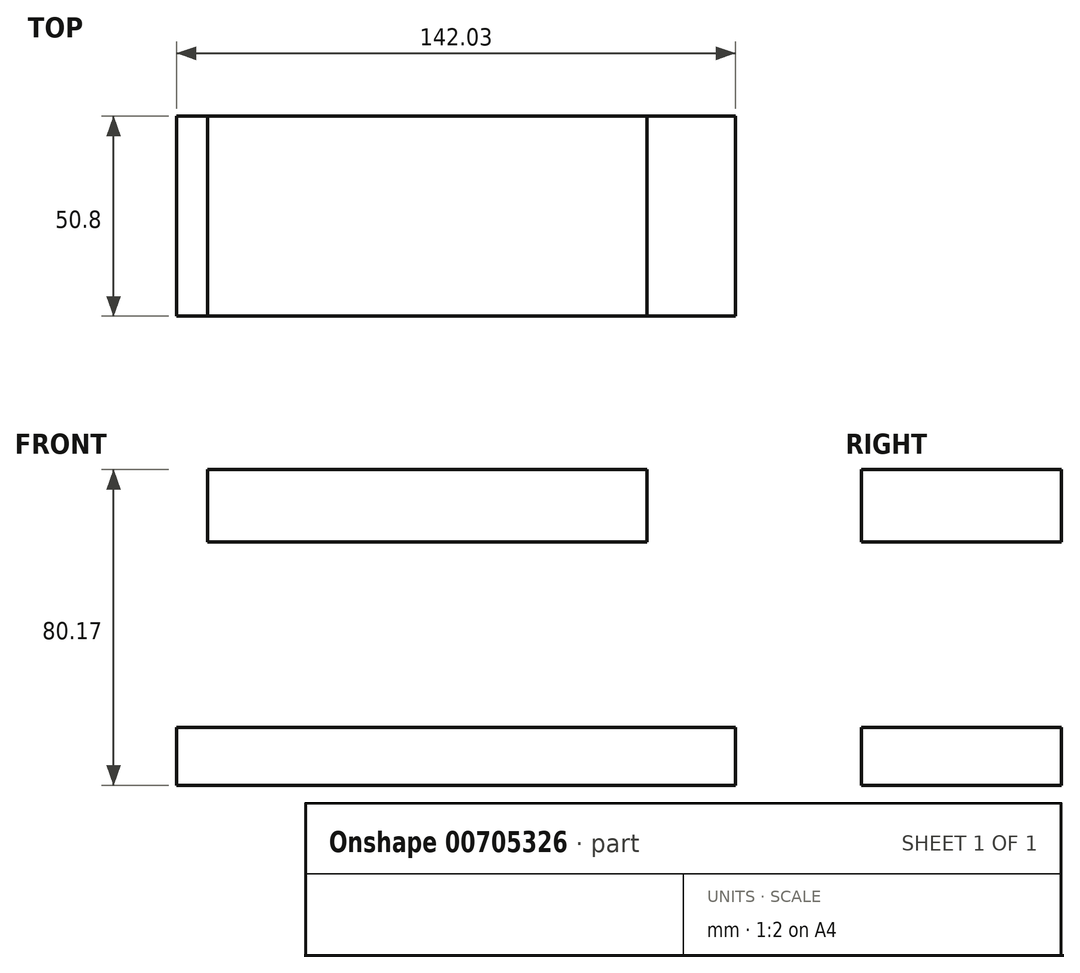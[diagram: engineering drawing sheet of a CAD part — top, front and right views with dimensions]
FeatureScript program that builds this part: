
annotation { "Feature Type Name" : "Feature", "Feature Type Description" : "" }
export const myFeature = defineFeature(function(context is Context, id is Id, definition is map)
    precondition{}
    {
        {
            var Q0;
            Q0=qCreatedBy(makeId("Front.planeOp"),FACE);
            var sketch = newSketch(context, id + "F0", { "sketchPlane" : qUnion([Q0])});
            skLineSegment(sketch, "E0.bottom", {"start": v(52.72, 35.9) * mm, "end": v(-58.98, 35.9) * mm});
            skLineSegment(sketch, "E0.top", {"start": v(52.72, 17.59) * mm, "end": v(-58.98, 17.59) * mm});
            skLineSegment(sketch, "E0.left", {"start": v(52.72, 35.9) * mm, "end": v(52.72, 17.59) * mm});
            skLineSegment(sketch, "E0.right", {"start": v(-58.98, 35.9) * mm, "end": v(-58.98, 17.59) * mm});
            skSolve(sketch);
        }
        {
            var Q0;
            Q0=makeQuery(id+"F0.imprint","IMPRINT",FACE,{"disambiguationData":[TD([[makeQuery(id+"F0.imprint","IMPRINT",EDGE,{"derivedFrom":sQuery(id+"F0.wireOp",EDGE,"E0.bottom")}),1.0]])]});
            extrude(context, id + "F1", {"entities" : qUnion([Q0]), "depth" : 25.4 * mm, "offsetDistance" : 25.4 * mm});
        }
        {
            var Q0;
            Q0=makeQuery(id+"F1.opExtrude","CAP_FACE",FACE,{"disambiguationData":[OSD([sQuery(id+"F0.wireOp",EDGE,"E0.bottom"),sQuery(id+"F0.wireOp",EDGE,"E0.top"),sQuery(id+"F0.wireOp",EDGE,"E0.left"),sQuery(id+"F0.wireOp",EDGE,"E0.right")])],"isStart":false});
            extrude(context, id + "F2", {"entities" : qUnion([Q0]), "operationType" : NewBodyOperationType.ADD, "depth" : 25.4 * mm, "offsetDistance" : 25.4 * mm});
        }
        {
            var Q0;
            Q0=qCreatedBy(makeId("Front.planeOp"),FACE);
            var sketch = newSketch(context, id + "F3", { "sketchPlane" : qUnion([Q0])});
            skLineSegment(sketch, "E1.right", {"start": v(70.44, -2.53) * mm, "end": v(70.44, 0) * mm});
            skLineSegment(sketch, "E2.bottom", {"start": v(-66.8, -29.56) * mm, "end": v(75.24, -29.56) * mm});
            skLineSegment(sketch, "E2.top", {"start": v(-66.8, -44.27) * mm, "end": v(75.24, -44.27) * mm});
            skLineSegment(sketch, "E2.left", {"start": v(-66.8, -29.56) * mm, "end": v(-66.8, -44.27) * mm});
            skLineSegment(sketch, "E2.right", {"start": v(75.24, -29.56) * mm, "end": v(75.24, -44.27) * mm});
            skSolve(sketch);
        }
        {
            var Q0;
            Q0=makeQuery(id+"F3.imprint","IMPRINT",FACE,{"disambiguationData":[TD([[makeQuery(id+"F3.imprint","IMPRINT",EDGE,{"derivedFrom":sQuery(id+"F3.wireOp",EDGE,"E2.bottom")}),-1.0]])]});
            extrude(context, id + "F4", {"entities" : qUnion([Q0]), "depth" : 25.4 * mm, "offsetDistance" : 25.4 * mm});
        }
        {
            var Q0;
            Q0=makeQuery(id+"F4.opExtrude","CAP_FACE",FACE,{"disambiguationData":[OSD([sQuery(id+"F3.wireOp",EDGE,"E2.bottom"),sQuery(id+"F3.wireOp",EDGE,"E2.top"),sQuery(id+"F3.wireOp",EDGE,"E2.left"),sQuery(id+"F3.wireOp",EDGE,"E2.right")])],"isStart":false});
            extrude(context, id + "F5", {"entities" : qUnion([Q0]), "operationType" : NewBodyOperationType.ADD, "depth" : 25.4 * mm, "offsetDistance" : 25.4 * mm});
        }
    });
